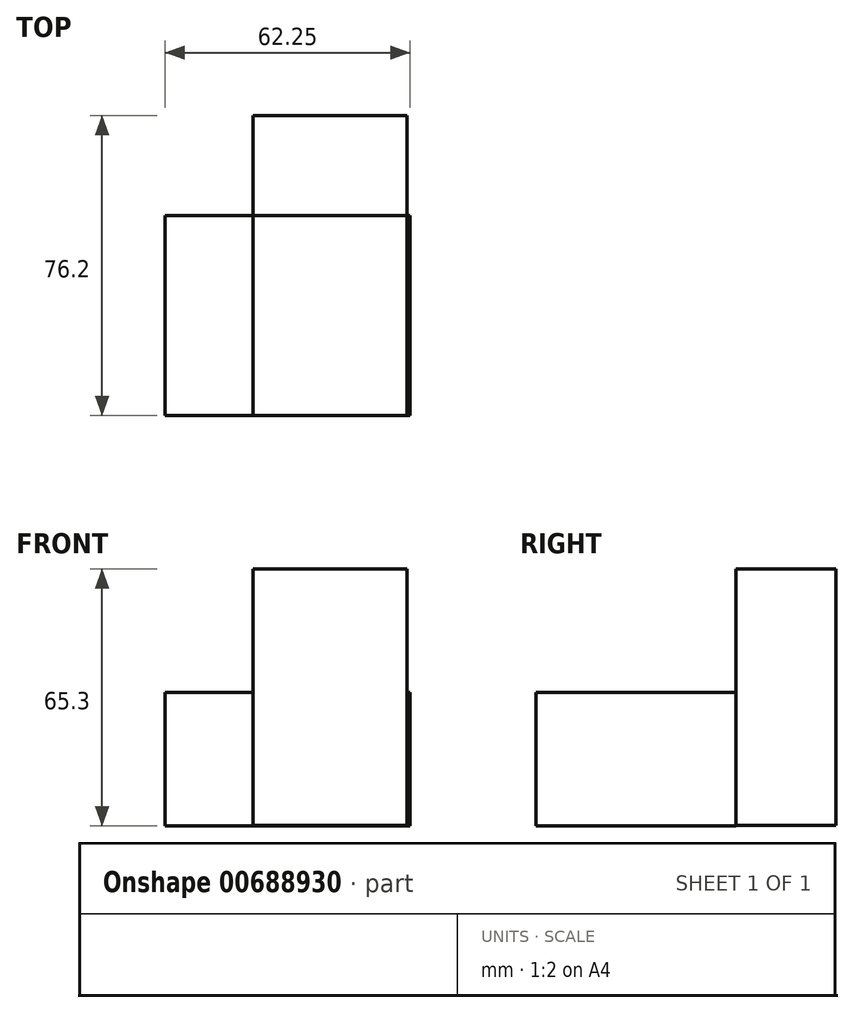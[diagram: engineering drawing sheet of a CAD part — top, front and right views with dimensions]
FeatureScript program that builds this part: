
annotation { "Feature Type Name" : "Feature", "Feature Type Description" : "" }
export const myFeature = defineFeature(function(context is Context, id is Id, definition is map)
    precondition{}
    {
        {
            var Q0;
            Q0=qCreatedBy(makeId("Front.planeOp"),FACE);
            var sketch = newSketch(context, id + "F0", { "sketchPlane" : qUnion([Q0])});
            skLineSegment(sketch, "E0.bottom", {"start": v(-37.33, 31.41) * mm, "end": v(1.81, 31.41) * mm});
            skLineSegment(sketch, "E0.top", {"start": v(-37.33, -33.7) * mm, "end": v(1.81, -33.7) * mm});
            skLineSegment(sketch, "E0.left", {"start": v(-37.33, 31.41) * mm, "end": v(-37.33, -33.7) * mm});
            skLineSegment(sketch, "E0.right", {"start": v(1.81, 31.41) * mm, "end": v(1.81, -33.7) * mm});
            skSolve(sketch);
        }
        {
            var Q0;
            Q0=makeQuery(id+"F0.imprint","IMPRINT",FACE,{"disambiguationData":[TD([[makeQuery(id+"F0.imprint","IMPRINT",EDGE,{"derivedFrom":sQuery(id+"F0.wireOp",EDGE,"E0.bottom")}),-1.0]])]});
            extrude(context, id + "F1", {"entities" : qUnion([Q0]), "depth" : 25.4 * mm, "offsetDistance" : 25.4 * mm});
        }
        {
            var Q0;
            Q0=makeQuery(id+"F1.opExtrude","CAP_FACE",FACE,{"disambiguationData":[OSD([sQuery(id+"F0.wireOp",EDGE,"E0.bottom"),sQuery(id+"F0.wireOp",EDGE,"E0.top"),sQuery(id+"F0.wireOp",EDGE,"E0.left"),sQuery(id+"F0.wireOp",EDGE,"E0.right")])],"isStart":false});
            var sketch = newSketch(context, id + "F2", { "sketchPlane" : qUnion([Q0])});
            skSolve(sketch);
        }
        {
            var Q0;
            Q0=makeQuery(id+"F2.imprint","IMPRINT",FACE,{"disambiguationData":[TD([[makeQuery(id+"F2.imprint","IMPRINT",EDGE,{"derivedFrom":makeQuery(id+"F1.opExtrude","CAP_EDGE",EDGE,{"disambiguationData":[OSD([sQuery(id+"F0.wireOp",EDGE,"E0.bottom")])],"isStart":false})}),-1.0]])]});
            var sketch = newSketch(context, id + "F3", { "sketchPlane" : qUnion([Q0])});
            skLineSegment(sketch, "E1.bottom", {"start": v(2.58, 0) * mm, "end": v(-59.67, 0) * mm});
            skLineSegment(sketch, "E1.top", {"start": v(2.58, -33.9) * mm, "end": v(-59.67, -33.9) * mm});
            skLineSegment(sketch, "E1.left", {"start": v(2.58, 0) * mm, "end": v(2.58, -33.9) * mm});
            skLineSegment(sketch, "E1.right", {"start": v(-59.67, 0) * mm, "end": v(-59.67, -33.9) * mm});
            skSolve(sketch);
        }
        {
            var Q0;
            Q0=makeQuery(id+"F3.imprint","IMPRINT",FACE,{"disambiguationData":[TD([[makeQuery(id+"F3.imprint","IMPRINT",EDGE,{"derivedFrom":sQuery(id+"F3.wireOp",EDGE,"E1.top")}),-1.0]])]});
            extrude(context, id + "F4", {"entities" : qUnion([Q0]), "depth" : 25.4 * mm, "offsetDistance" : 25.4 * mm});
        }
        {
            var Q0;
            Q0=makeQuery(id+"F4.opExtrude","CAP_FACE",FACE,{"disambiguationData":[OSD([sQuery(id+"F0.wireOp",EDGE,"E0.top"),sQuery(id+"F0.wireOp",EDGE,"E0.left"),sQuery(id+"F0.wireOp",EDGE,"E0.right"),sQuery(id+"F3.wireOp",EDGE,"E1.bottom"),sQuery(id+"F3.wireOp",EDGE,"E1.top"),sQuery(id+"F3.wireOp",EDGE,"E1.left"),sQuery(id+"F3.wireOp",EDGE,"E1.right")])],"isStart":false});
            extrude(context, id + "F5", {"entities" : qUnion([Q0]), "operationType" : NewBodyOperationType.ADD, "depth" : 25.4 * mm, "offsetDistance" : 25.4 * mm});
        }
    });
